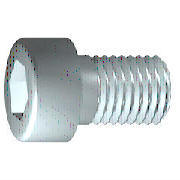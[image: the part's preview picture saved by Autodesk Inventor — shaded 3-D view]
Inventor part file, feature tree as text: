
AUTODESK INVENTOR PART (.ipt)
format: ipt  version: 2020 (Build 240168000, 168)  size: 188,416 bytes
history: native  units: mm (DEFAULTED — no unit token found)
features: sketch x2, extrude x1, plane x1, fillet x1
ambient origin geometry x7: Origin, YZ Plane, XY Plane, X Axis, Y Axis, Z Axis, Center Point
bodies: Solid1 (feature_tree), Body (feature_tree)
feature tree (5):
  extrude  "Slot"  Depth=3.0mm
  plane  "Work Plane1"
  fillet  "Fillet2"  Radius=3.0mm
  sketch  "Sketch1"  dims[d1=18.0mm d2=0.306825mm d3=3.0mm]
  sketch  "Sketch2"  dims[d4=1.3mm d5=60.0deg d6=3.0mm d7=3.0mm d8=2.886751mm d9=5.5mm d10=90.0deg d11=10.0mm d12=0.0mm d13=18.0mm d14=0.0mm d15=0.306725mm d16=0.306725mm d17=0.3mm d19=0.0mm d26=30.0mm d27=45.0deg d28=0.0mm d29=0.0mm d30=0.1mm]
